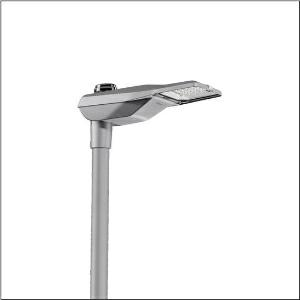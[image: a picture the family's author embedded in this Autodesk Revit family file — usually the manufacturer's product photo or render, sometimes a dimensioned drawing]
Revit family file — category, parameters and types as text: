
# Revit family: streetlight_sl_21_micro___pl52_5xe5h37n08cb_9265
name_source: partatom
category: Lighting Fixtures
units: mm (PartAtom-declared; Revit-internal decimal feet)

## family parameters
Cut with Voids When Loaded = No
Host = Face
Light Source = No
Part Type = Normal
Room Calculation Point = No
Round Connector Dimension = Use Diameter
Shared = No

## types (1)
- --- (1 x LED, 2250 lm, 15.8 W, 3000K)
    Apparent Load = 16 VA
    CIE Flux Codes = 27 59 98 100 100
    Color Rendering = 70
    Color Temperature = 3000K
    Default Elevation = 1800 mm
    Description = Streetlight SL 21 micro, mast luminaire, primary light control with lens, of PMMA, primary optical cover: cover, of toughened safety glass, transparent, light distribution: PL52, light emission: direct distribution, primary light characteristic: asymmetric, installation type: post-top, LED, 3G 1.5mm², High Power LED, rated luminous flux: 2.250lm, luminous efficacy: 142lm/W, light colour: 730, colour temperature: 3000K, control: overheat protection, presetting dimming linear, constant luminous flux control, time-dependent luminous flux control, flexible luminous flux parameterisation, mains connection: 230..240V, AC, 50/60Hz, connection cable pre-assembled, cable length: 6,5m, wiring characteristics: H07RN-F, start of lifetime: 16W, end of service life: 16W, reduction: 8W, luminaire housing, of diecast aluminium (EN AC-44300), powder-coated, Siteco® metallic grey (DB 702S), corrosivity category C5 mid according to DIN EN ISO 12944, multi-level sealing system, sealing non-destructively replaceable, inclination adjustable: 0°, 5°, 10°, 15°, length: 528mm, width: 235mm, height: 110mm, spigot size: 76/60mm (post-top), protection rating (complete): IP66, insulation class (complete): insulation class I (protective earthing), certification: CE, ENEC, ENEC+, VDE, impact resistance: IK09, permissible operating ambient temperature for outdoor applications: -40..+50°C, standard-compliant lighting for roads and squares, packaging unit: 1 piece

Light Distribution: PL52
    Height = 110 mm
    Lamp = 1 x LED
    Lamp Light Flux = 2250 lm
    Lamp Power = 15.8 W
    Lamp count = 1
    Length = 528 mm
    Luminous efficacy = 142 lm/W
    Manufacturer = Siteco
    ModVariant = No
    Model = 5XE5H37N08CB
    Number of Poles = 1
    OnlyDefault = Yes
    Power Factor = 1
    Product Name = Streetlight SL 21 micro | PL52
    Product group = mast luminaire | pylon top
    ProductGroupID = 6100
    Protection Class = Protection class I
    Protection Degree = IP 66
    RLX_Detail_Level = 1
    RLX_Emergency_Light_Flux = 0 lm
    RLX_Emergency_Type = 0
    RLX_Emergency_Type_DB = No
    RlxData = <blob elided: 108457 chars, md5=c97709a2>
    Socket = socket
    Standby Power = 0 W
    System Light Flux = 2250 lm
    System Power = 16 W
    Type Comments = factory setting: luminous flux: 100 % | dim-lin: 254 | 300 mA
    Type Image = l_1294375.jpg
    URL = http://relux.com
    VarID = @adj_086607
    Voltage = 0 V
    Weight = 0.00 kg
    Width = 235 mm

## geometry (parser evidence)
native form markers: Blend x4, Sweep x9
no freeform markers — native parametric forms only
